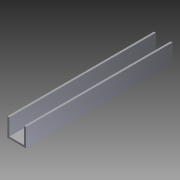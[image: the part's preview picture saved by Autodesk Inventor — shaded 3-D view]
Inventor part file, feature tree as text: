
AUTODESK INVENTOR PART (.ipt)
format: ipt  version: 2012 (Build 160160000, 160)  size: 79,872 bytes
history: native  units: in
note: dims shown in document units (in); Inventor stores cm internally (conversion verified against a paired STEP export)
features: extrude x1, sketch x1
ambient origin geometry x8: Origin, YZ Plane, XZ Plane, XY Plane, X Axis, Y Axis, Z Axis, Center Point
bodies: Solid1 (feature_tree)
feature tree (2):
  extrude  "Extrusion1"  Depth=0.125in
  sketch  "Sketch1"  dims[d0=0.125in d2=0.125in d3=0.125in d4=1.25in d5=1.25in d6=9.875in d7=0.0in]
